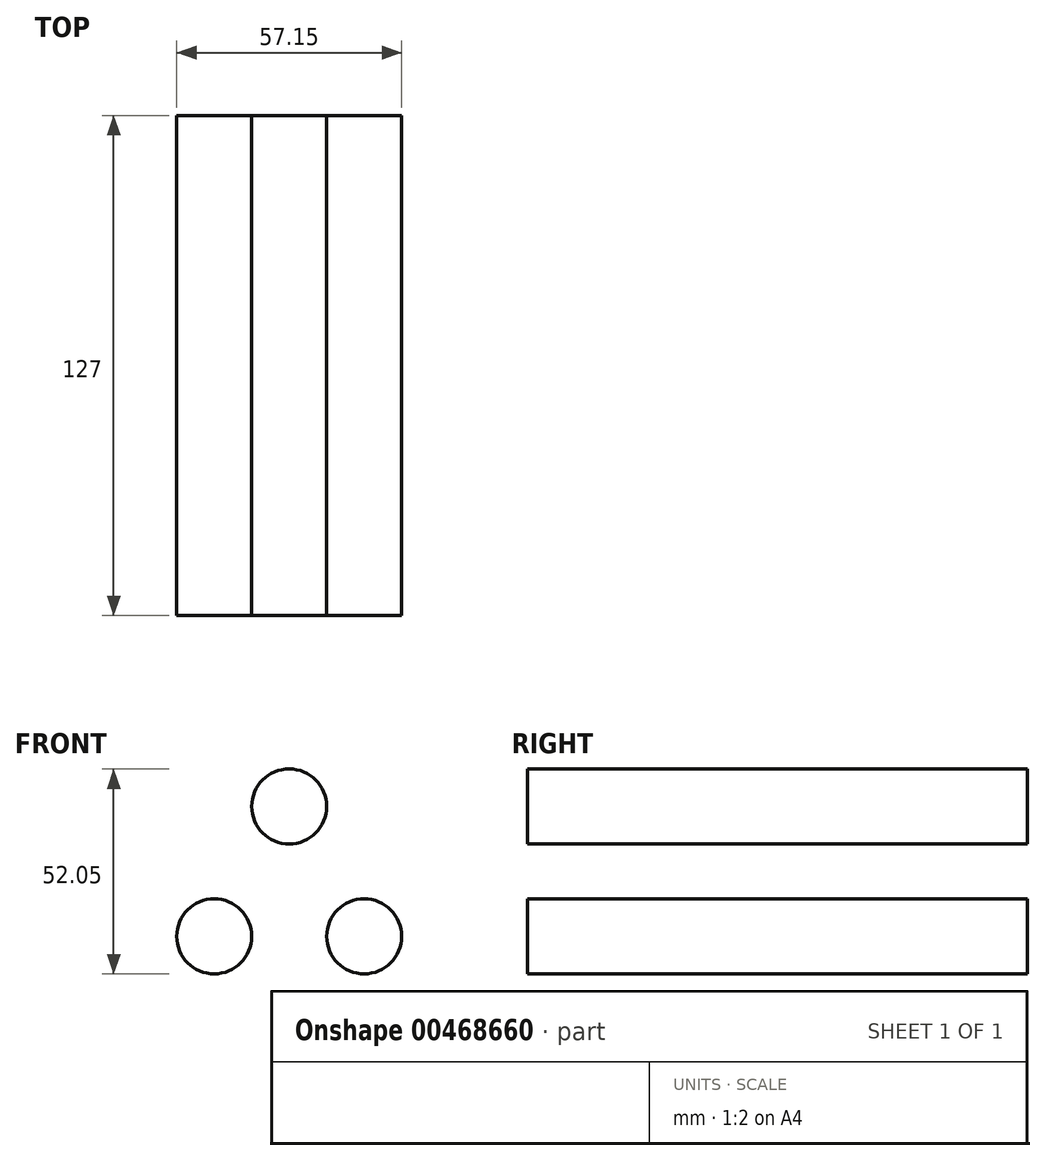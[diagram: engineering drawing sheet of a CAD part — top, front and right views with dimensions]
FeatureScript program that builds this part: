
annotation { "Feature Type Name" : "Feature", "Feature Type Description" : "" }
export const myFeature = defineFeature(function(context is Context, id is Id, definition is map)
    precondition{}
    {
        {
            var Q0;
            Q0=qCreatedBy(makeId("Front.planeOp"),FACE);
            var sketch = newSketch(context, id + "F0", { "sketchPlane" : qUnion([Q0])});
            skCircle(sketch, "E0", {"center": v(-24.1, 0) * mm, "radius": 9.53 * mm});
            skCircle(sketch, "E1", {"center": v(14, 0) * mm, "radius": 9.53 * mm});
            skCircle(sketch, "E2", {"center": v(-5.06, 33) * mm, "radius": 9.53 * mm});
            skSolve(sketch);
        }
        {
            var Q0;
            Q0 = qSketchRegion(id + "F0", true);
            extrude(context, id + "F1", {"entities" : qUnion([Q0]), "endBound" : BoundingType.SYMMETRIC, "depth" : 127 * mm});
        }
    });
